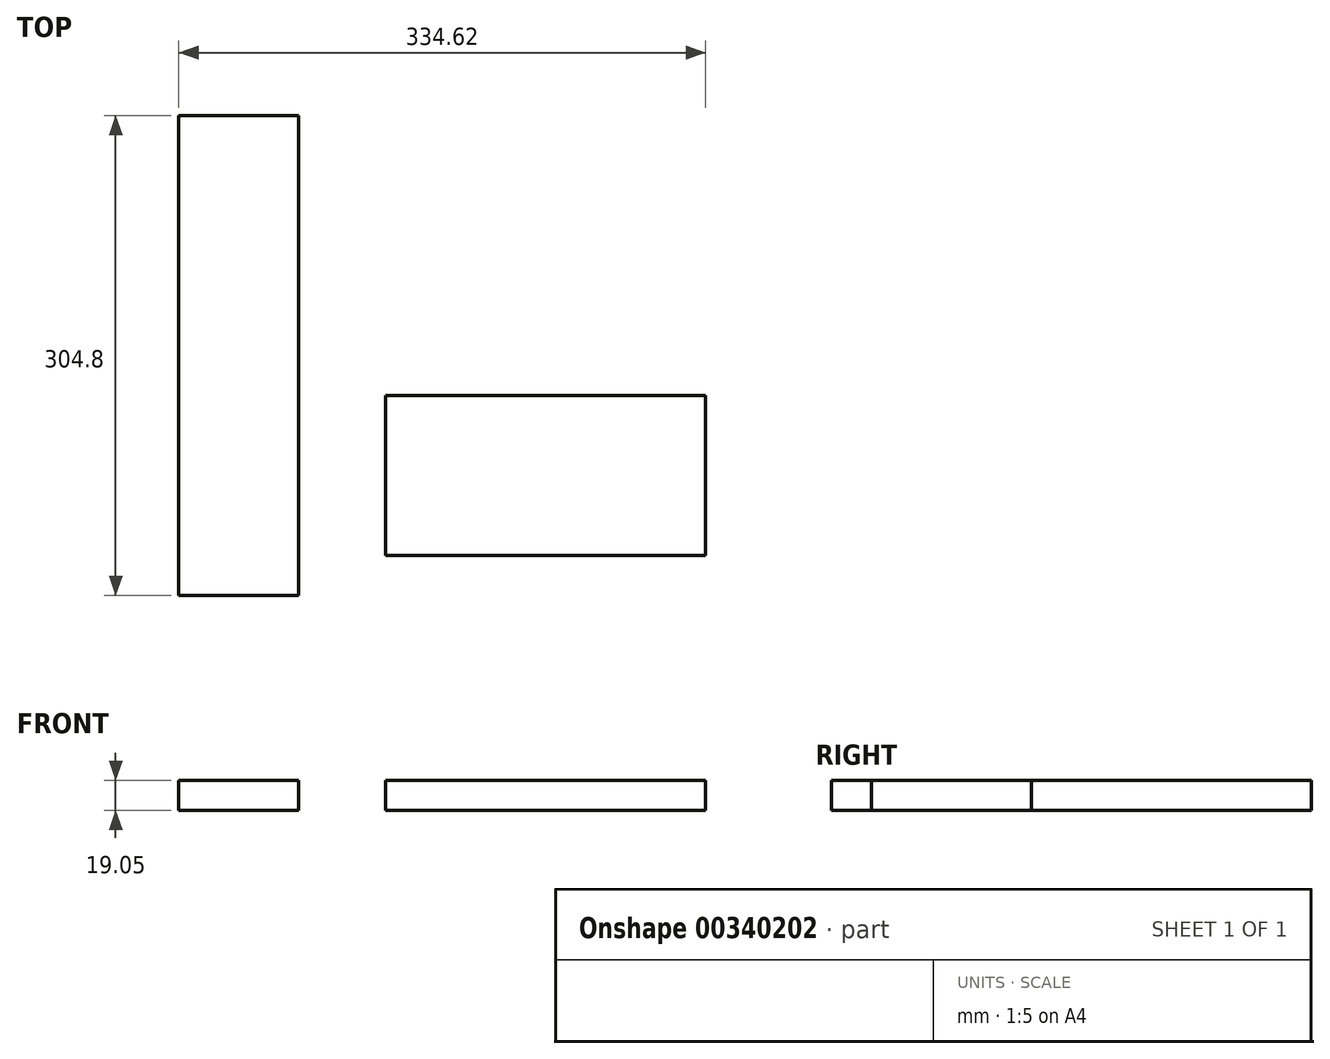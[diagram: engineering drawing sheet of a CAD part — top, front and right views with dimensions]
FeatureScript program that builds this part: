
annotation { "Feature Type Name" : "Feature", "Feature Type Description" : "" }
export const myFeature = defineFeature(function(context is Context, id is Id, definition is map)
    precondition{}
    {
        {
            var Q0;
            Q0=qCreatedBy(makeId("Top.planeOp"),FACE);
            var sketch = newSketch(context, id + "F0", { "sketchPlane" : qUnion([Q0])});
            skLineSegment(sketch, "E0.bottom", {"start": v(12.6, 263.2) * mm, "end": v(-63.6, 263.2) * mm});
            skLineSegment(sketch, "E0.top", {"start": v(12.6, -41.6) * mm, "end": v(-63.6, -41.6) * mm});
            skLineSegment(sketch, "E0.left", {"start": v(12.6, 263.2) * mm, "end": v(12.6, -41.6) * mm});
            skLineSegment(sketch, "E0.right", {"start": v(-63.6, 263.2) * mm, "end": v(-63.6, -41.6) * mm});
            skLineSegment(sketch, "E1.bottom", {"start": v(271.02, 85.34) * mm, "end": v(67.82, 85.34) * mm});
            skLineSegment(sketch, "E1.top", {"start": v(271.02, -16.26) * mm, "end": v(67.82, -16.26) * mm});
            skLineSegment(sketch, "E1.left", {"start": v(271.02, 85.34) * mm, "end": v(271.02, -16.26) * mm});
            skLineSegment(sketch, "E1.right", {"start": v(67.82, 85.34) * mm, "end": v(67.82, -16.26) * mm});
            skSolve(sketch);
        }
        {
            var Q0;
            Q0=makeQuery(id+"F0.imprint","IMPRINT",FACE,{"disambiguationData":[TD([[makeQuery(id+"F0.imprint","IMPRINT",EDGE,{"derivedFrom":sQuery(id+"F0.wireOp",EDGE,"E0.bottom")}),1.0]])]});
            var Q1;
            Q1=makeQuery(id+"F0.imprint","IMPRINT",FACE,{"disambiguationData":[TD([[makeQuery(id+"F0.imprint","IMPRINT",EDGE,{"derivedFrom":sQuery(id+"F0.wireOp",EDGE,"E1.bottom")}),1.0]])]});
            extrude(context, id + "F1", {"entities" : qUnion([Q0, Q1]), "depth" : 19.05 * mm});
        }
    });
